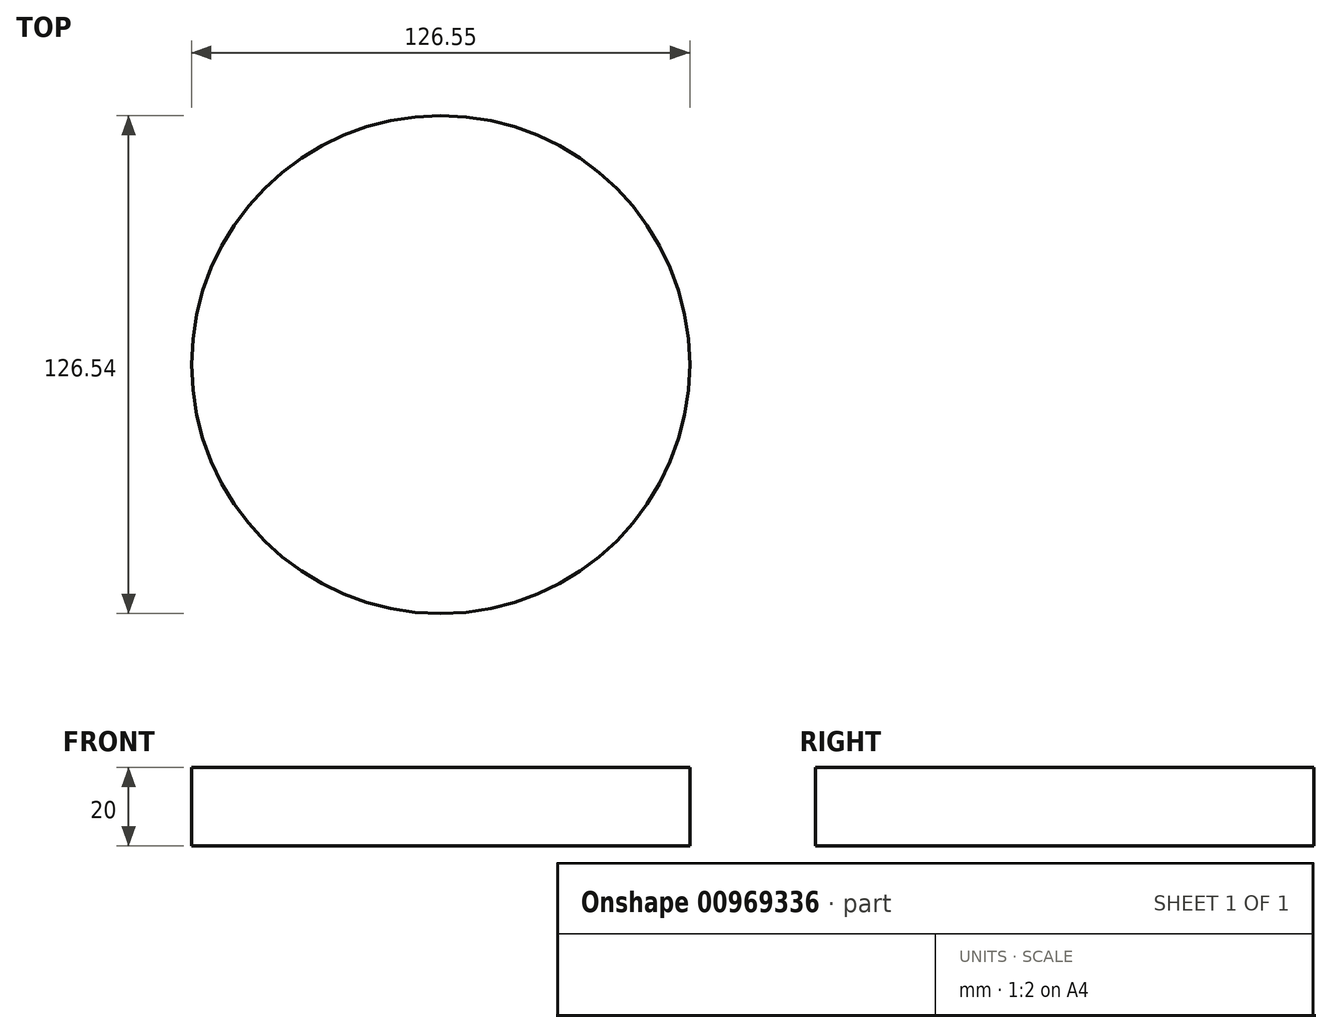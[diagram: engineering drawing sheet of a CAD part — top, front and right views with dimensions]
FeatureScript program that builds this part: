
annotation { "Feature Type Name" : "Feature", "Feature Type Description" : "" }
export const myFeature = defineFeature(function(context is Context, id is Id, definition is map)
    precondition{}
    {
        {
            var Q0;
            Q0=qCreatedBy(makeId("Top.planeOp"),FACE);
            var sketch = newSketch(context, id + "F0", { "sketchPlane" : qUnion([Q0])});
            skCircle(sketch, "E0", {"center": v(50.02, 0) * mm, "radius": 63.27 * mm});
            skSolve(sketch);
        }
        {
            var Q0;
            Q0=makeQuery(id+"F0.imprint","IMPRINT",FACE,{"disambiguationData":[TD([[makeQuery(id+"F0.imprint","IMPRINT",EDGE,{"derivedFrom":sQuery(id+"F0.wireOp",EDGE,"E0")}),1.0]])]});
            extrude(context, id + "F1", {"entities" : qUnion([Q0]), "depth" : 20 * mm, "offsetDistance" : 25.4 * mm});
        }
    });
